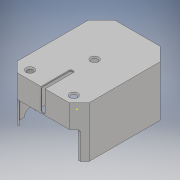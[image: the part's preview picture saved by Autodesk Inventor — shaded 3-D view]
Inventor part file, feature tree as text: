
AUTODESK INVENTOR PART (.ipt)
format: ipt  version: 2017 (Build 210142000, 142)  size: 472,576 bytes
history: native  units: mm
features: sketch x11, extrude x10, other x6, fillet x4, hole x3, projected_geometry x2
ambient origin geometry x8: Origin, YZ Plane, XZ Plane, XY Plane, X Axis, Y Axis, Z Axis, Center Point
bodies: Body1 (feature_tree)
feature tree (36):
  other  "Твердое тело1"
  sketch  "Эскиз1"
  extrude  "Выдавливание1"  Depth=60.0mm
  extrude  "Выдавливание2"  Depth=80.0mm
  fillet  "Сопряжение1"  Radius=11.0mm
  extrude  "Выдавливание3"  Depth=11.0mm
  extrude  "Выдавливание4"  Depth=8.5mm
  extrude  "Выдавливание5"  Depth=8.5mm
  other  "Комбинировать1"
  hole  "Отверстие4"  [1 undecoded]
  hole  "Отверстие5"  [1 undecoded]
  hole  "Отверстие6"  [1 undecoded]
  fillet  "Сопряжение2"  Radius=11.0mm
  fillet  "Сопряжение3"  Radius=1.2mm
  extrude  "Выдавливание6"  Depth=1.0mm TaperAngle=0.0deg
  extrude  "Выдавливание7"  Depth=43.0mm TaperAngle=0.0deg
  extrude  "Выдавливание8"  Depth=1.0mm
  other  "Комбинировать2"
  fillet  "Сопряжение4"  Radius=3.5mm
  sketch  "Эскиз8"
  sketch  "Эскиз9"
  sketch  "Эскиз10"
  extrude  "Выдавливание10"  Depth=25.0mm
  other  "РабПлоскость2"
  extrude  "Выдавливание12"  Depth=18.0mm TaperAngle=0.0deg
  other  "Твердое тело2"
  sketch  "Эскиз2"
  sketch  "Эскиз3"
  sketch  "Эскиз4"
  other  "Твердое тело3"
  sketch  "Эскиз5"
  sketch  "Эскиз6"
  sketch  "Эскиз11"
  projected_geometry  "Спроецированная петля1"
  sketch  "Эскиз13"
  projected_geometry  "Спроецированная петля2"
note: 3 required parameter values undecoded (feature->parameter linkage not recoverable at this tier; creation-order binding heuristic only, values carry confidence <= 0.55)
